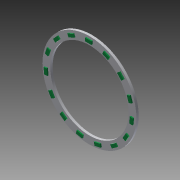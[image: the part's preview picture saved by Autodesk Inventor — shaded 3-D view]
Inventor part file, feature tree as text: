
AUTODESK INVENTOR PART (.ipt)
format: ipt  version: 2018 (Build 220112000, 112)  size: 171,008 bytes
history: native  units: mm
features: extrude x2, sketch x2, pattern_circular x1
ambient origin geometry x8: Origin, YZ Plane, XZ Plane, XY Plane, X Axis, Y Axis, Z Axis, Center Point
bodies: Solid1 (feature_tree)
feature tree (5):
  extrude  "Extrusion1"  Depth=50.0mm
  extrude  "Extrusion2"  Depth=2.0mm
  pattern_circular  "Circular Pattern1"  [2 undecoded]
  sketch  "Sketch1"  dims[d0=60.0mm d1=50.0mm]
  sketch  "Sketch2"  dims[d2=1.5mm d3=0.0mm d4=2.0mm d5=26.5mm d6=4.0mm d7=0.75mm d8=0.0mm d9=150.0mm d10=360.0deg]
note: 2 required parameter values undecoded (feature->parameter linkage not recoverable at this tier; creation-order binding heuristic only, values carry confidence <= 0.55)
